FCSTD DOCUMENT  (FreeCAD 1.0R39319 (Git))
Label: session2_drawing3
License: All rights reserved
LicenseURL: https://en.wikipedia.org/wiki/All_rights_reserved
objects: Sketcher::SketchObject×1, PartDesign::Body×1
note: 3 computed .brp shape members not serialized (recipe doc carries the construction recipe); baked Part::Feature solids carry a one-line shape summary decoded from their .brp

FEATURE [Sketcher::SketchObject] Sketch
  ArcFitTolerance = 1e-06
  AttachmentSupport = -> [XY_Plane]
  FullyConstrained = true
  MakeInternals = false
  MapMode = 5
  sketch-geometry (24):
    g0: ArcOfCircle CenterX=0 CenterY=-83.7906 CenterZ=0 NormalX=0 NormalY=0 NormalZ=1 AngleXU=0 Radius=40 StartAngle=2.38214 EndAngle=7.04264
    g1: ArcOfCircle CenterX=0 CenterY=26.2094 CenterZ=0 NormalX=0 NormalY=0 NormalZ=1 AngleXU=0 Radius=22 StartAngle=0.391465 EndAngle=2.75013
    g2: ArcOfCircle CenterX=-50.7649 CenterY=-35.5939 CenterZ=0 NormalX=0 NormalY=0 NormalZ=1 AngleXU=0 Radius=30 StartAngle=5.52373 EndAngle=6.89468
    g3: ArcOfCircle CenterX=50.7649 CenterY=-35.5939 CenterZ=0 NormalX=0 NormalY=0 NormalZ=1 AngleXU=0 Radius=30 StartAngle=2.53009 EndAngle=3.90105
    g4: LineSegment StartX=-29.5792 StartY=12.2094 StartZ=0 EndX=-20.3357 EndY=34.6033 EndZ=0
    g5: ArcOfCircle CenterX=0 CenterY=0 CenterZ=0 NormalX=0 NormalY=0 NormalZ=1 AngleXU=0 Radius=32 StartAngle=5.67169 EndAngle=6.67465
    g6: ArcOfCircle CenterX=0 CenterY=0 CenterZ=0 NormalX=0 NormalY=0 NormalZ=1 AngleXU=0 Radius=32 StartAngle=2.75013 EndAngle=3.75309
    g7: LineSegment StartX=29.5792 StartY=12.2094 StartZ=0 EndX=20.3357 EndY=34.6033 EndZ=0
    g8: ArcOfCircle CenterX=0 CenterY=26.2094 CenterZ=0 NormalX=0 NormalY=0 NormalZ=1 AngleXU=0 Radius=22 StartAngle=2e-16 EndAngle=3.14159
    g9: ArcOfCircle CenterX=5e-16 CenterY=-1.79063 CenterZ=0 NormalX=0 NormalY=0 NormalZ=1 AngleXU=0 Radius=22 StartAngle=3.14159 EndAngle=6.28319
    g10: LineSegment StartX=22 StartY=26.2094 StartZ=0 EndX=22 EndY=-1.79063 EndZ=0
    g11: LineSegment StartX=-22 StartY=26.2094 StartZ=0 EndX=-22 EndY=-1.79063 EndZ=0
    g12: ArcOfCircle CenterX=0 CenterY=-73.7906 CenterZ=0 NormalX=0 NormalY=0 NormalZ=1 AngleXU=0 Radius=12 StartAngle=6.2117 EndAngle=9.49627
    g13: ArcOfCircle CenterX=0 CenterY=-101.791 CenterZ=0 NormalX=0 NormalY=0 NormalZ=1 AngleXU=0 Radius=10 StartAngle=3.21308 EndAngle=6.2117
    g14: LineSegment StartX=-11.9693 StartY=-74.6478 StartZ=0 EndX=-9.97446 EndY=-102.505 EndZ=0
    g15: LineSegment StartX=11.9693 StartY=-74.6478 StartZ=0 EndX=9.97446 EndY=-102.505 EndZ=0
    g16: ArcOfCircle CenterX=0 CenterY=26.2094 CenterZ=0 NormalX=0 NormalY=0 NormalZ=1 AngleXU=0 Radius=10 StartAngle=1e-16 EndAngle=3.14159
    g17: ArcOfCircle CenterX=5e-16 CenterY=-1.79063 CenterZ=0 NormalX=0 NormalY=0 NormalZ=1 AngleXU=0 Radius=12 StartAngle=3.14159 EndAngle=6.28319
    g18: LineSegment StartX=-12 StartY=-1.79063 StartZ=0 EndX=-12 EndY=9.38095 EndZ=0
    g19: LineSegment StartX=-10 StartY=12.2094 StartZ=0 EndX=-10 EndY=26.2094 EndZ=0
    g20: LineSegment StartX=12 StartY=-1.79063 StartZ=0 EndX=12 EndY=9.38095 EndZ=0
    g21: LineSegment StartX=10 StartY=12.2094 StartZ=0 EndX=10 EndY=26.2094 EndZ=0
    g22: ArcOfCircle CenterX=-9 CenterY=9.38095 CenterZ=0 NormalX=0 NormalY=0 NormalZ=1 AngleXU=0 Radius=3 StartAngle=1.91063 EndAngle=3.14159
    g23: ArcOfCircle CenterX=9 CenterY=9.38095 CenterZ=0 NormalX=0 NormalY=0 NormalZ=1 AngleXU=0 Radius=3 StartAngle=0 EndAngle=1.23096
  constraints (60):
    c: PointOnObject(g0,g-2)
    c: Diameter(g0) = 80
    c: PointOnObject(g1,g-2)
    c: Radius(g2) = 30
    c: Equal(g2,g3)
    c: Tangent(g1,g4) = 1.5708
    c: Tangent(g6,g2) = 1.5708
    c: Tangent(g6,g4) = 1.5708
    c: PointOnObject(g7,g5)
    c: Tangent(g5,g7) = -1.5708
    c: Tangent(g5,g3) = 1.5708
    c: Radius(g6) = 32
    c: Radius(g5) = 32
    c: Coincident(g6,g-1)
    c: Coincident(g5,g6)
    c: Tangent(g0,g3) = 1.5708
    c: Tangent(g0,g2) = 1.5708
    c: DistanceY(g7,g1) = 14
    c: Tangent(g1,g7) = -1.5708
    c: Tangent(g8,g10) = 1.5708
    c: Tangent(g8,g11) = -1.5708
    c: Tangent(g9,g10) = 1.5708
    c: Tangent(g9,g11) = -1.5708
    c: Equal(g8,g9)
    c: Vertical(g11)
    c: Coincident(g8,g1)
    c: Radius(g8) = 22
    c: DistanceY(g9,g1) = 28
    c: Radius(g1) = 22
    c: PointOnObject(g12,g-2)
    c: PointOnObject(g13,g-2)
    c: Tangent(g13,g15) = 1.5708
    c: Tangent(g12,g14) = -1.5708
    c: Tangent(g12,g15) = 1.5708
    c: Radius(g13) = 10
    c: Radius(g12) = 12
    c: DistanceY(g13,g12) = 28
    c: DistanceY(g0,g12) = 10
    c: Tangent(g13,g14) = -1.5708
    c: DistanceY(g13,g1) = 128
    c: Coincident(g16,g1)
    c: Coincident(g17,g9)
    c: Vertical(g18)
    c: Vertical(g20)
    c: Diameter(g17) = 24
    c: Diameter(g16) = 20
    c: Vertical(g19)
    c: Vertical(g21)
    c: Coincident(g19,g22)
    c: Coincident(g21,g23)
    c: Radius(g22) = 3
    c: Radius(g23) = 3
    c: Tangent(g17,g20) = -1.5708
    c: Tangent(g17,g18) = 1.5708
    c: Tangent(g16,g19) = 1.5708
    c: Tangent(g16,g21) = -1.5708
    c: DistanceY(g21,g1) = 14
    c: DistanceY(g19,g1) = 14
    c: Tangent(g22,g18) = 1.5708
    c: Tangent(g23,g20) = -1.5708
FEATURE [PartDesign::Body] Body
  AllowCompound = false
  Group = -> [Sketch]
  Origin = -> Origin
